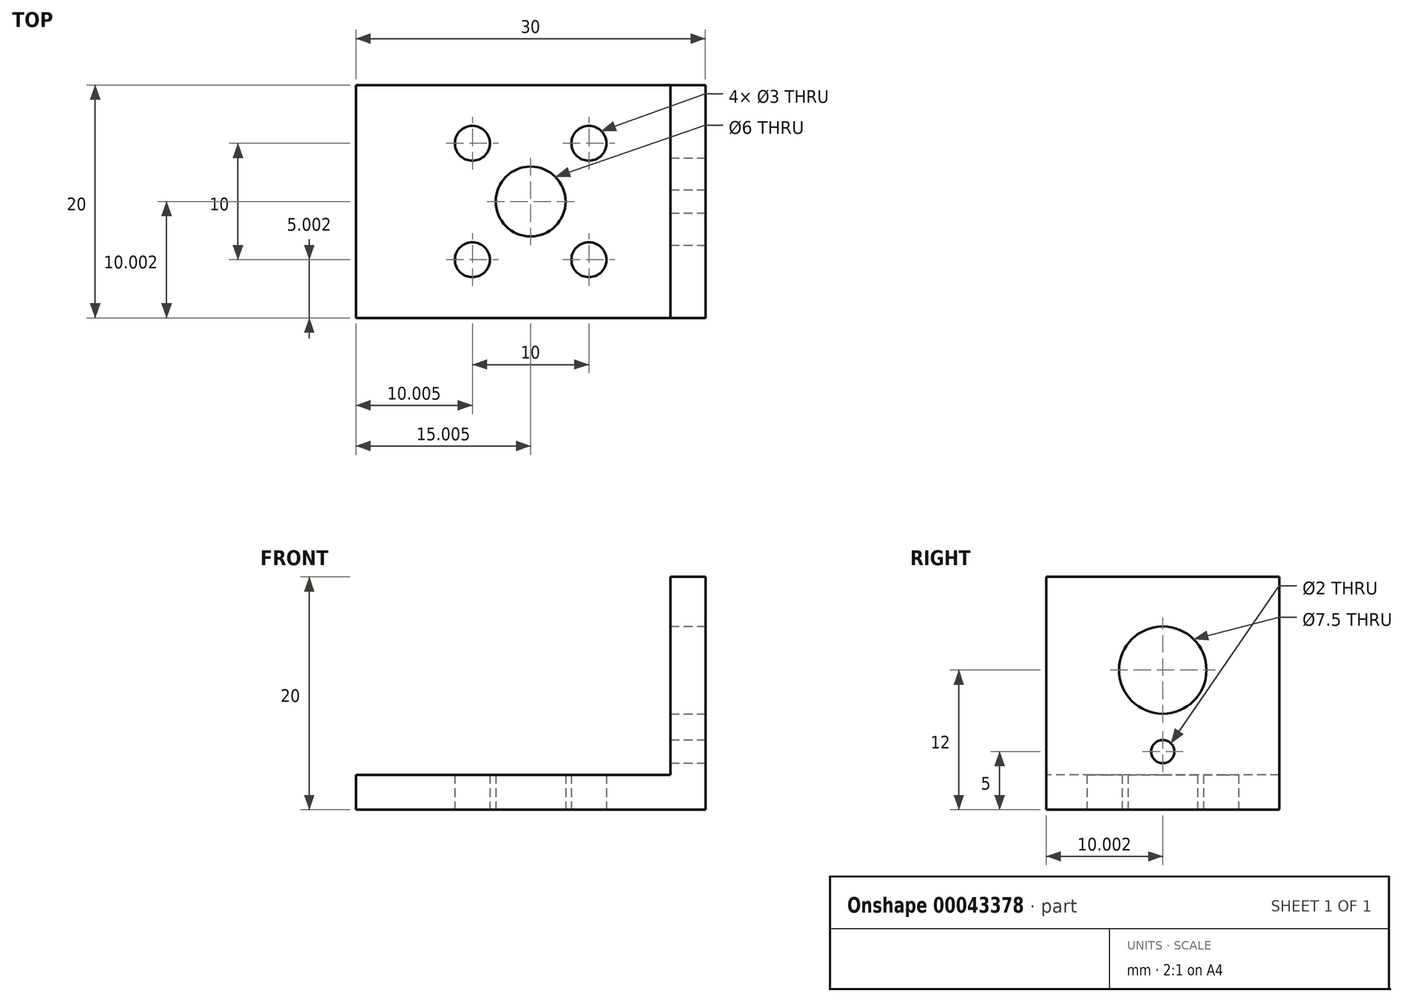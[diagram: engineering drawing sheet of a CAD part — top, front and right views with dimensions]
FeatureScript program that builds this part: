
annotation { "Feature Type Name" : "Feature", "Feature Type Description" : "" }
export const myFeature = defineFeature(function(context is Context, id is Id, definition is map)
    precondition{}
    {
        {
            var Q0;
            Q0=qCreatedBy(makeId("Top.planeOp"),FACE);
            var sketch = newSketch(context, id + "F0", { "sketchPlane" : qUnion([Q0])});
            skLineSegment(sketch, "E0.bottom", {"start": v(-17.45, 9.5) * mm, "end": v(12.55, 9.5) * mm});
            skLineSegment(sketch, "E0.top", {"start": v(-17.45, -10.5) * mm, "end": v(12.55, -10.5) * mm});
            skLineSegment(sketch, "E0.left", {"start": v(-17.45, 9.5) * mm, "end": v(-17.45, -10.5) * mm});
            skLineSegment(sketch, "E0.right", {"start": v(12.55, 9.5) * mm, "end": v(12.55, -10.5) * mm});
            skLineSegment(sketch, "E1", {"start": v(-17.45, -0.5) * mm, "end": v(12.55, -0.5) * mm, "construction": true});
            skLineSegment(sketch, "E2", {"start": v(-2.45, 9.5) * mm, "end": v(-2.45, -10.5) * mm, "construction": true});
            skPoint(sketch, "E3", {"position": v(-2.45, -0.5) * mm});
            skCircle(sketch, "E4", {"center": v(-2.45, -0.5) * mm, "radius": 3 * mm});
            skLineSegment(sketch, "E5.bottom", {"start": v(-7.45, 4.5) * mm, "end": v(2.55, 4.5) * mm, "construction": true});
            skLineSegment(sketch, "E5.top", {"start": v(-7.45, -5.5) * mm, "end": v(2.55, -5.5) * mm, "construction": true});
            skLineSegment(sketch, "E5.left", {"start": v(-7.45, 4.5) * mm, "end": v(-7.45, -5.5) * mm, "construction": true});
            skLineSegment(sketch, "E5.right", {"start": v(2.55, 4.5) * mm, "end": v(2.55, -5.5) * mm, "construction": true});
            skLineSegment(sketch, "E6", {"start": v(-2.45, 4.5) * mm, "end": v(-2.45, -5.5) * mm, "construction": true});
            skLineSegment(sketch, "E7", {"start": v(-7.45, -0.5) * mm, "end": v(2.55, -0.5) * mm, "construction": true});
            skCircle(sketch, "E8", {"center": v(2.55, 4.5) * mm, "radius": 1.5 * mm});
            skCircle(sketch, "E9.1.1", {"center": v(-7.45, 4.5) * mm, "radius": 1.5 * mm});
            skCircle(sketch, "E9.2.1", {"center": v(-7.45, -5.5) * mm, "radius": 1.5 * mm});
            skCircle(sketch, "E9.3.1", {"center": v(2.55, -5.5) * mm, "radius": 1.5 * mm});
            skLineSegment(sketch, "E10", {"start": v(9.55, 9.5) * mm, "end": v(9.55, -10.5) * mm});
            skSolve(sketch);
        }
        {
            var Q0;
            {var subQ2=sQuery(id+"F0.wireOp",EDGE,"E0.left");Q0=makeQuery(id+"F0.imprint","IMPRINT",FACE,{"disambiguationData":[TD([[makeQuery(id+"F0.imprint","IMPRINT",EDGE,{"derivedFrom":subQ2}),1.0]])]});}
            extrude(context, id + "F1", {"entities" : qUnion([Q0]), "depth" : 3 * mm});
        }
        {
            var Q0;
            {var subQ1=sQuery(id+"F0.wireOp",EDGE,"E0.right");Q0=makeQuery(id+"F0.imprint","IMPRINT",FACE,{"disambiguationData":[TD([[makeQuery(id+"F0.imprint","IMPRINT",EDGE,{"derivedFrom":subQ1}),-1.0]])]});}
            extrude(context, id + "F2", {"entities" : qUnion([Q0]), "operationType" : NewBodyOperationType.ADD, "depth" : 20 * mm});
        }
        {
            var Q0;
            Q0=makeQuery(id+"F2.opExtrude","SWEPT_FACE",FACE,{"disambiguationData":[OSD([sQuery(id+"F0.wireOp",EDGE,"E0.right")])]});
            var sketch = newSketch(context, id + "F3", { "sketchPlane" : qUnion([Q0])});
            skLineSegment(sketch, "E11.bottom", {"start": v(-10.5, 20) * mm, "end": v(9.5, 20) * mm, "construction": true});
            skLineSegment(sketch, "E11.top", {"start": v(-10.5, 0) * mm, "end": v(9.5, 0) * mm, "construction": true});
            skLineSegment(sketch, "E11.left", {"start": v(-10.5, 20) * mm, "end": v(-10.5, 0) * mm, "construction": true});
            skLineSegment(sketch, "E11.right", {"start": v(9.5, 20) * mm, "end": v(9.5, 0) * mm, "construction": true});
            skLineSegment(sketch, "E12", {"start": v(-0.5, 20) * mm, "end": v(-0.5, 0) * mm, "construction": true});
            skCircle(sketch, "E13", {"center": v(-0.5, 12) * mm, "radius": 3.75 * mm});
            skCircle(sketch, "E14", {"center": v(-0.5, 5) * mm, "radius": 1 * mm});
            skCircle(sketch, "E15", {"center": v(-0.5, -2.5) * mm, "radius": 1 * mm});
            skSolve(sketch);
        }
        {
            var Q0;
            Q0 = qSketchRegion(id + "F3", true);
            extrude(context, id + "F4", {"entities" : qUnion([Q0]), "operationType" : NewBodyOperationType.REMOVE, "oppositeDirection" : true, "depth" : 3 * mm});
        }
    });
